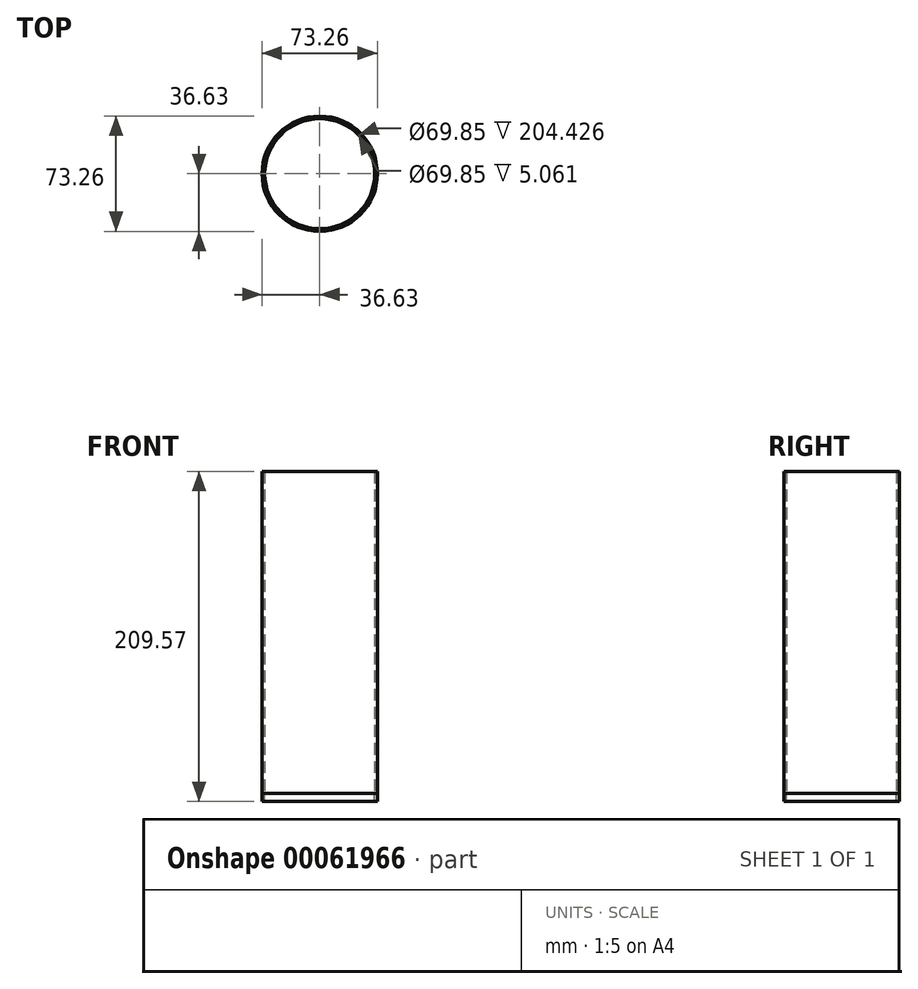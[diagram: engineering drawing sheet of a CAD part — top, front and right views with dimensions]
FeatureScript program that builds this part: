
annotation { "Feature Type Name" : "Feature", "Feature Type Description" : "" }
export const myFeature = defineFeature(function(context is Context, id is Id, definition is map)
    precondition{}
    {
        {
            var Q0;
            Q0=qCreatedBy(makeId("Top.planeOp"),FACE);
            var sketch = newSketch(context, id + "F0", { "sketchPlane" : qUnion([Q0])});
            skCircle(sketch, "E0", {"center": v(0, 0) * mm, "radius": 34.92 * mm});
            skSolve(sketch);
        }
        {
            var Q0;
            Q0=makeQuery(id+"F0.imprint","IMPRINT",FACE,{"disambiguationData":[TD([[makeQuery(id+"F0.imprint","IMPRINT",EDGE,{"derivedFrom":sQuery(id+"F0.wireOp",EDGE,"E0")}),1.0]])]});
            extrude(context, id + "F1", {"entities" : qUnion([Q0]), "depth" : 5.14 * mm});
        }
        {
            var Q0;
            Q0=makeQuery(id+"F1.opExtrude","CAP_FACE",FACE,{"disambiguationData":[OSD([sQuery(id+"F0.wireOp",EDGE,"E0")])],"isStart":false});
            var sketch = newSketch(context, id + "F2", { "sketchPlane" : qUnion([Q0])});
            skCircle(sketch, "E1", {"center": v(0, 0) * mm, "radius": 36.63 * mm});
            skSolve(sketch);
        }
        {
            var Q0;
            Q0=makeQuery(id+"F2.imprint","IMPRINT",FACE,{"disambiguationData":[TD([[makeQuery(id+"F2.imprint","IMPRINT",EDGE,{"derivedFrom":sQuery(id+"F2.wireOp",EDGE,"E1")}),1.0]])]});
            extrude(context, id + "F3", {"entities" : qUnion([Q0]), "depth" : 204.43 * mm});
        }
        {
            var Q0;
            Q0=makeQuery(id+"F3.opExtrude","CAP_FACE",FACE,{"disambiguationData":[OSD([sQuery(id+"F0.wireOp",EDGE,"E0"),sQuery(id+"F2.wireOp",EDGE,"E1")])],"isStart":true});
            extrude(context, id + "F4", {"entities" : qUnion([Q0]), "depth" : 5.06 * mm});
        }
    });
